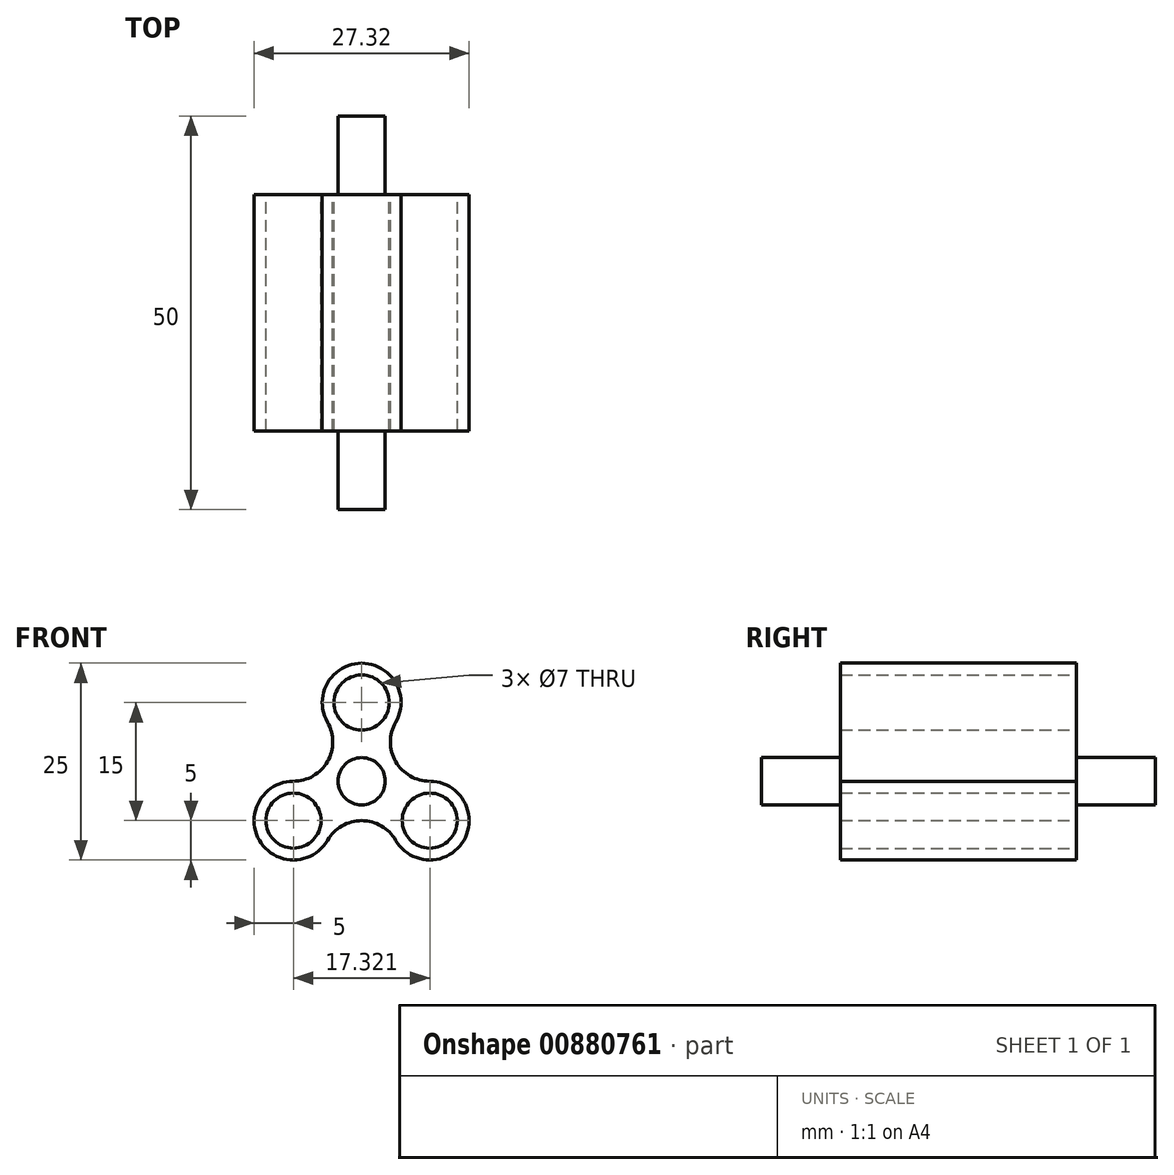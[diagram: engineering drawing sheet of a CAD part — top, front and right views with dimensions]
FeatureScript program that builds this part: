
annotation { "Feature Type Name" : "Feature", "Feature Type Description" : "" }
export const myFeature = defineFeature(function(context is Context, id is Id, definition is map)
    precondition{}
    {
        {
            var Q0;
            Q0=qCreatedBy(makeId("Front.planeOp"),FACE);
            var sketch = newSketch(context, id + "F0", { "sketchPlane" : qUnion([Q0])});
            skArc(sketch, "E0", {"start": v(4.33, 7.5) * mm, "mid": v(0, 15) * mm, "end": v(-4.33, 7.5) * mm});
            skArc(sketch, "E1.1.0", {"start": v(4.33, 7.5) * mm, "mid": v(4.33, 2.5) * mm, "end": v(8.66, 0) * mm});
            skCircle(sketch, "E1.2.0", {"center": v(8.66, -5) * mm, "radius": 5 * mm});
            skPoint(sketch, "E1.center", {"position": v(0, 0) * mm});
            skLineSegment(sketch, "E1.anchor1", {"start": v(0, 0) * mm, "end": v(0, 10) * mm, "construction": true});
            skLineSegment(sketch, "E1.anchor2", {"start": v(0, 0) * mm, "end": v(0, 10) * mm, "construction": true});
            skArc(sketch, "E2.1.3.0", {"start": v(4.33, -7.5) * mm, "mid": v(0, -5) * mm, "end": v(-4.33, -7.5) * mm});
            skCircle(sketch, "E3.1.4.0", {"center": v(-8.66, -5) * mm, "radius": 5 * mm});
            skArc(sketch, "E3.1.5.0", {"start": v(-8.66, 0) * mm, "mid": v(-4.33, 2.5) * mm, "end": v(-4.33, 7.5) * mm});
            skCircle(sketch, "E3.1.6.0", {"center": v(0, 10) * mm, "radius": 5 * mm});
            skCircle(sketch, "E4", {"center": v(0, 10) * mm, "radius": 3.5 * mm});
            skCircle(sketch, "E5", {"center": v(8.66, -5) * mm, "radius": 3.5 * mm});
            skCircle(sketch, "E6", {"center": v(-8.66, -5) * mm, "radius": 3.5 * mm});
            skPoint(sketch, "E7", {"position": v(17.44, 0) * mm});
            skSolve(sketch);
        }
        {
            var Q0;
            Q0 = qSketchRegion(id + "F0", true);
            extrude(context, id + "F1", {"entities" : qUnion([Q0]), "depth" : 30 * mm, "offsetDistance" : 25 * mm});
        }
        {
            var Q0;
            Q0=qCreatedBy(makeId("Front.planeOp"),FACE);
            var sketch = newSketch(context, id + "F2", { "sketchPlane" : qUnion([Q0])});
            skCircle(sketch, "E8", {"center": v(0, 0) * mm, "radius": 3 * mm});
            skSolve(sketch);
        }
        {
            var Q0;
            Q0 = qSketchRegion(id + "F2", true);
            extrude(context, id + "F3", {"entities" : qUnion([Q0]), "operationType" : NewBodyOperationType.ADD, "depth" : 40 * mm, "offsetDistance" : 25 * mm, "hasSecondDirection" : true, "secondDirectionOppositeDirection" : true, "secondDirectionDepth" : 10 * mm});
        }
    });
